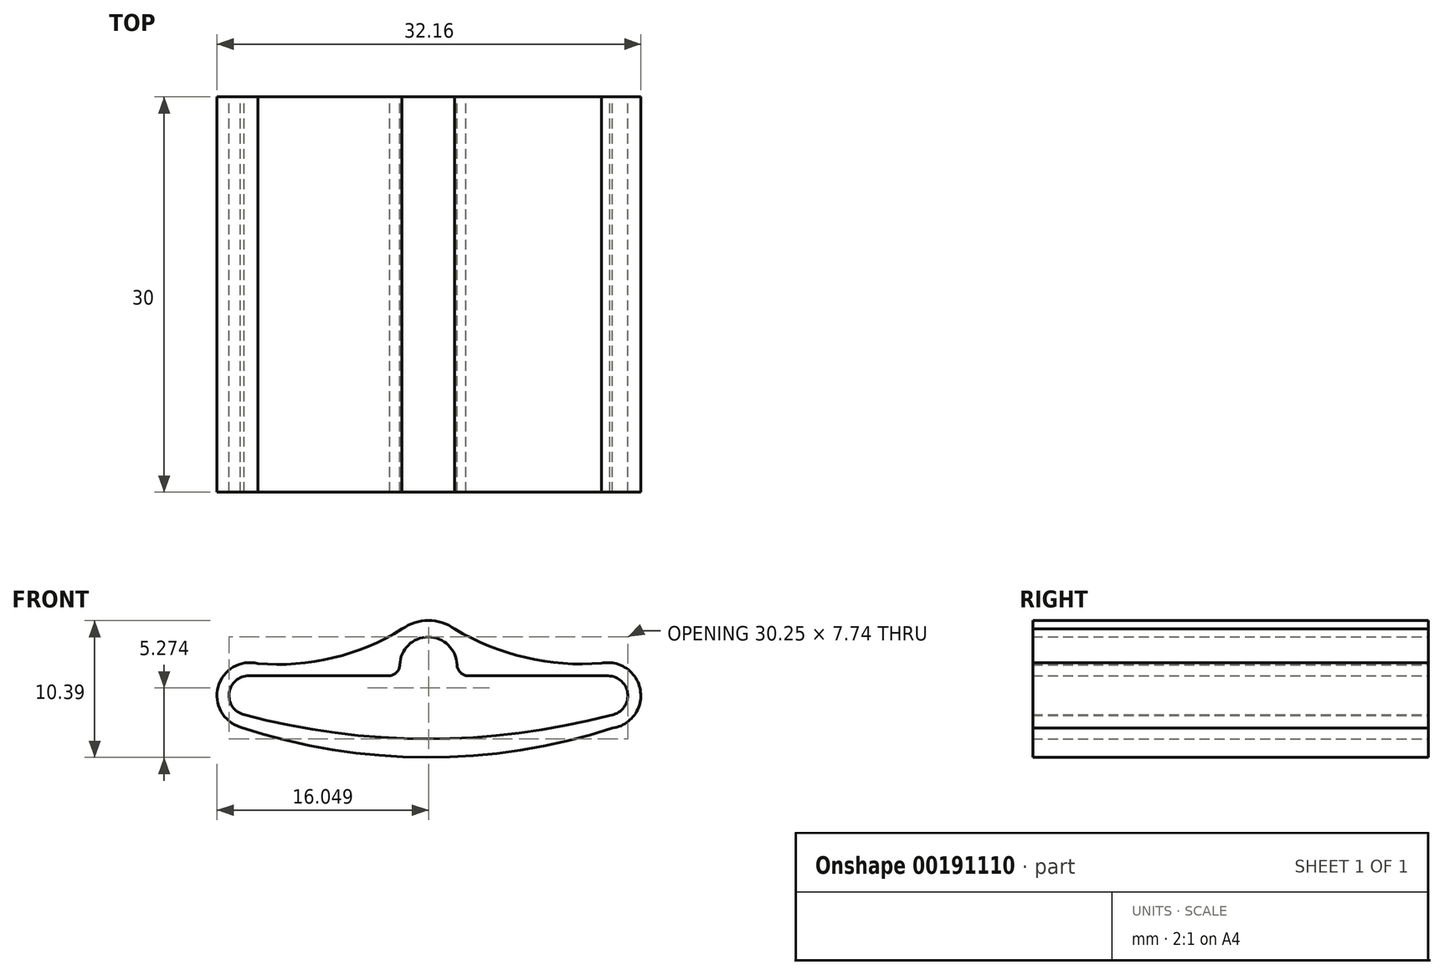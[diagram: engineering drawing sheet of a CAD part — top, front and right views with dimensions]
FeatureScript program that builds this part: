
annotation { "Feature Type Name" : "Feature", "Feature Type Description" : "" }
export const myFeature = defineFeature(function(context is Context, id is Id, definition is map)
    precondition{}
    {
        {
            var Q0;
            Q0=qCreatedBy(makeId("Front.planeOp"),FACE);
            var sketch = newSketch(context, id + "F0", { "sketchPlane" : qUnion([Q0])});
            skArc(sketch, "E0", {"start": v(-13.62, 1.5) * mm, "mid": v(-15.11, 0.18) * mm, "end": v(-13.97, -1.46) * mm});
            skArc(sketch, "E1", {"start": v(13.77, -1.5) * mm, "mid": v(15.13, 0.06) * mm, "end": v(13.63, 1.5) * mm});
            skLineSegment(sketch, "E2", {"start": v(-13.62, 1.5) * mm, "end": v(-2.93, 1.5) * mm});
            skArc(sketch, "E3", {"start": v(2.17, 2.33) * mm, "mid": v(0, 4.44) * mm, "end": v(-2.17, 2.33) * mm});
            skLineSegment(sketch, "E4", {"start": v(0, 4.44) * mm, "end": v(0, -3.3) * mm});
            skArc(sketch, "E5", {"start": v(-2.93, 1.5) * mm, "mid": v(-2.4, 1.77) * mm, "end": v(-2.17, 2.33) * mm});
            skArc(sketch, "E6", {"start": v(2.17, 2.33) * mm, "mid": v(2.38, 1.81) * mm, "end": v(2.84, 1.5) * mm});
            skLineSegment(sketch, "E7.trimOffspring", {"start": v(2.84, 1.5) * mm, "end": v(13.63, 1.5) * mm});
            skArc(sketch, "E8", {"start": v(-14.05, -1.44) * mm, "mid": v(-0.15, -3.3) * mm, "end": v(13.77, -1.5) * mm});
            skSolve(sketch);
        }
        {
            var Q0;
            Q0=qCreatedBy(makeId("Front.planeOp"),FACE);
            var sketch = newSketch(context, id + "F1", { "sketchPlane" : qUnion([Q0])});
            skArc(sketch, "E9", {"start": v(-12.94, 2.43) * mm, "mid": v(-15.95, 0.66) * mm, "end": v(-14.26, -2.4) * mm});
            skArc(sketch, "E10", {"start": v(13.97, -2.47) * mm, "mid": v(16.08, 0.42) * mm, "end": v(13.13, 2.45) * mm});
            skArc(sketch, "E11", {"start": v(2, 5.05) * mm, "mid": v(0, 5.7) * mm, "end": v(-2, 5.05) * mm});
            skArc(sketch, "E12", {"start": v(-13.63, 2.5) * mm, "mid": v(-7.6, 2.78) * mm, "end": v(-2, 5.05) * mm});
            skArc(sketch, "E13", {"start": v(2, 5.05) * mm, "mid": v(7.61, 2.83) * mm, "end": v(13.64, 2.5) * mm});
            skArc(sketch, "E14", {"start": v(-14.26, -2.4) * mm, "mid": v(-0.15, -4.7) * mm, "end": v(13.97, -2.47) * mm});
            skSolve(sketch);
        }
        {
            var Q0;
            Q0 = qSketchRegion(id + "F1", true);
            extrude(context, id + "F2", {"entities" : qUnion([Q0]), "depth" : 30 * mm});
        }
        {
            var Q0;
            Q0 = qSketchRegion(id + "F0", true);
            extrude(context, id + "F3", {"entities" : qUnion([Q0]), "operationType" : NewBodyOperationType.REMOVE, "endBound" : BoundingType.THROUGH_ALL, "depth" : 50 * mm});
        }
    });
